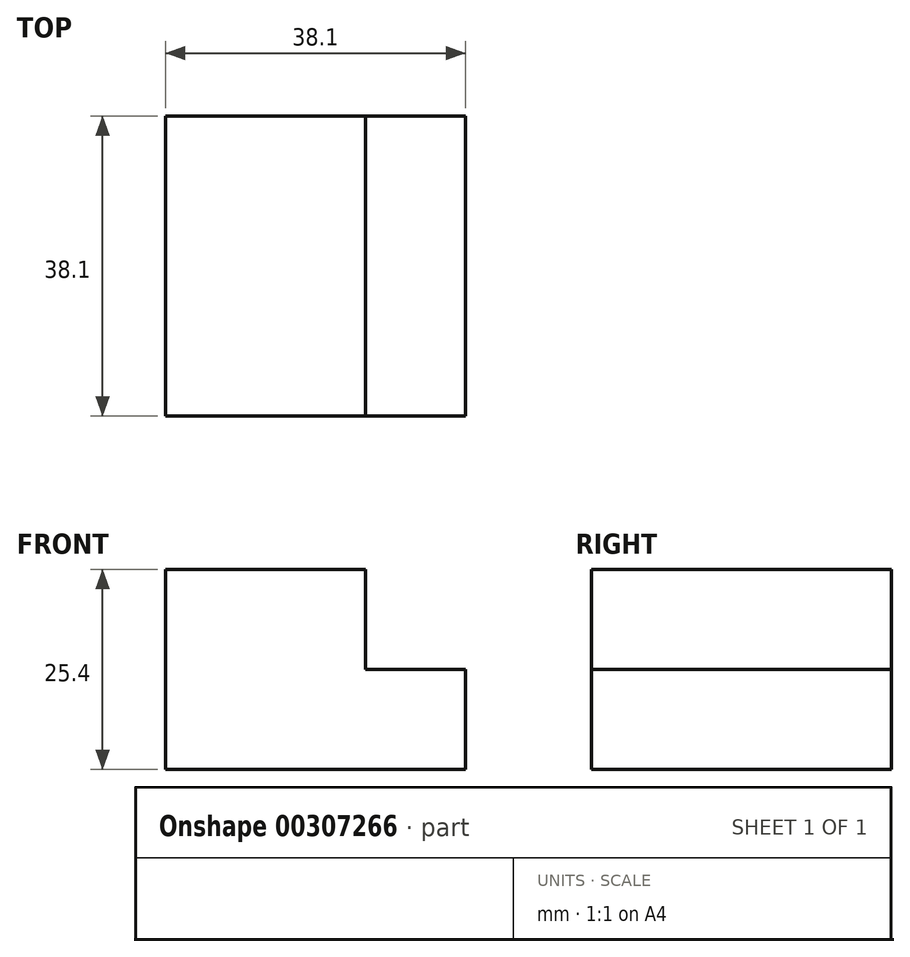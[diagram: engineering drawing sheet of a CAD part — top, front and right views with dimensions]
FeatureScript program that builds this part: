
annotation { "Feature Type Name" : "Feature", "Feature Type Description" : "" }
export const myFeature = defineFeature(function(context is Context, id is Id, definition is map)
    precondition{}
    {
        {
            var Q0;
            Q0=qCreatedBy(makeId("Front.planeOp"),FACE);
            var sketch = newSketch(context, id + "F0", { "sketchPlane" : qUnion([Q0])});
            skLineSegment(sketch, "E0", {"start": v(-37.3, -46.48) * mm, "end": v(0.8, -46.48) * mm});
            skLineSegment(sketch, "E1", {"start": v(0.8, -46.48) * mm, "end": v(0.8, -33.78) * mm});
            skLineSegment(sketch, "E2", {"start": v(0.8, -33.78) * mm, "end": v(-11.9, -33.78) * mm});
            skLineSegment(sketch, "E3", {"start": v(-11.9, -33.78) * mm, "end": v(-11.9, -21.08) * mm});
            skLineSegment(sketch, "E4", {"start": v(-11.9, -21.08) * mm, "end": v(-37.3, -21.08) * mm});
            skLineSegment(sketch, "E5", {"start": v(-37.3, -21.08) * mm, "end": v(-37.3, -46.48) * mm});
            skSolve(sketch);
        }
        {
            var Q0;
            Q0=makeQuery(id+"F0.imprint","IMPRINT",FACE,{"disambiguationData":[TD([[makeQuery(id+"F0.imprint","IMPRINT",EDGE,{"derivedFrom":sQuery(id+"F0.wireOp",EDGE,"E0")}),1.0]])]});
            extrude(context, id + "F1", {"entities" : qUnion([Q0]), "depth" : 38.1 * mm});
        }
    });
